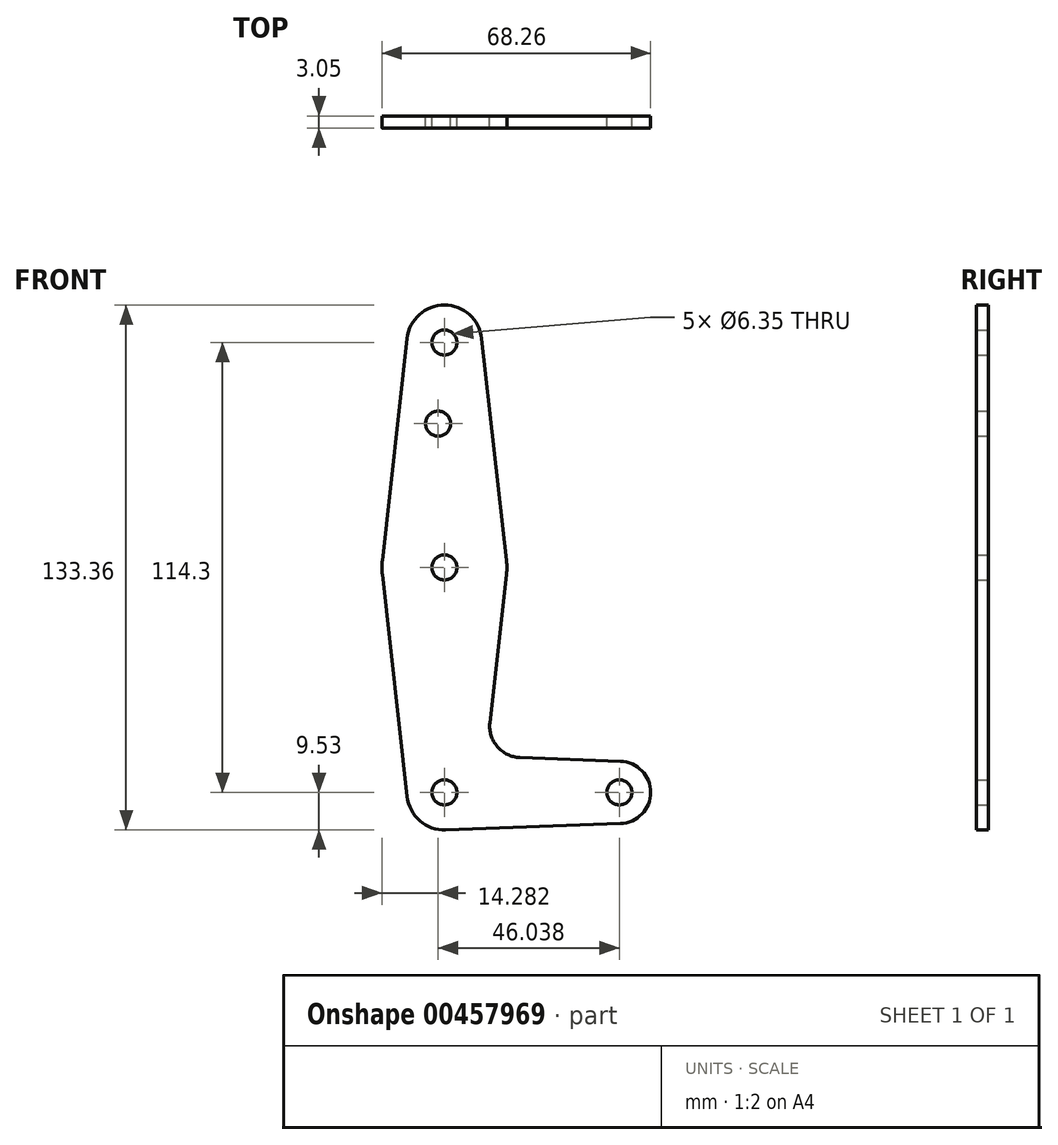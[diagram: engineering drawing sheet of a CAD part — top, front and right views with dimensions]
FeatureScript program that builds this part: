
annotation { "Feature Type Name" : "Feature", "Feature Type Description" : "" }
export const myFeature = defineFeature(function(context is Context, id is Id, definition is map)
    precondition{}
    {
        {
            var Q0;
            Q0=qCreatedBy(makeId("Front.planeOp"),FACE);
            var sketch = newSketch(context, id + "F0", { "sketchPlane" : qUnion([Q0])});
            skLineSegment(sketch, "E0", {"start": v(0, 0) * mm, "end": v(0, 114.3) * mm, "construction": true});
            skLineSegment(sketch, "E1", {"start": v(0, 0) * mm, "end": v(44.45, 0) * mm, "construction": true});
            skCircle(sketch, "E2", {"center": v(0, 114.3) * mm, "radius": 9.53 * mm});
            skCircle(sketch, "E3", {"center": v(44.45, 0) * mm, "radius": 7.94 * mm});
            skCircle(sketch, "E4", {"center": v(0, 0) * mm, "radius": 9.53 * mm});
            skCircle(sketch, "E5", {"center": v(0, 57.15) * mm, "radius": 15.88 * mm});
            skLineSegment(sketch, "E6", {"start": v(-9.47, 115.36) * mm, "end": v(-15.78, 58.91) * mm});
            skLineSegment(sketch, "E7", {"start": v(-15.78, 55.39) * mm, "end": v(-9.47, -1.06) * mm});
            skLineSegment(sketch, "E8", {"start": v(44.73, -7.93) * mm, "end": v(-3.54, -9.66) * mm});
            skLineSegment(sketch, "E9.MirrorCS", {"start": v(9.47, 115.36) * mm, "end": v(15.78, 58.91) * mm});
            skLineSegment(sketch, "E10.MirrorCS", {"start": v(15.78, 55.39) * mm, "end": v(11.56, 17.67) * mm});
            skLineSegment(sketch, "E11.MirrorCS", {"start": v(44.73, 7.93) * mm, "end": v(19.18, 8.85) * mm});
            skCircle(sketch, "E12", {"center": v(0, 114.3) * mm, "radius": 3.18 * mm});
            skCircle(sketch, "E13", {"center": v(-1.59, 93.68) * mm, "radius": 3.18 * mm});
            skCircle(sketch, "E14", {"center": v(0, 57.15) * mm, "radius": 3.18 * mm});
            skCircle(sketch, "E15", {"center": v(0, 0) * mm, "radius": 3.18 * mm});
            skCircle(sketch, "E16", {"center": v(44.45, 0) * mm, "radius": 3.18 * mm});
            skPoint(sketch, "E17.newPointA", {"position": v(9.47, -1.06) * mm});
            skPoint(sketch, "E17.newPointB", {"position": v(-3.54, 9.66) * mm});
            skArc(sketch, "E17.filletArc", {"start": v(11.56, 17.67) * mm, "mid": v(13.44, 11.6) * mm, "end": v(19.18, 8.85) * mm});
            skSolve(sketch);
        }
        {
            var Q0;
            Q0=makeQuery(id+"F0.imprint","IMPRINT",FACE,{"disambiguationData":[TD([[makeQuery(id+"F0.imprint","IMPRINT",EDGE,{"derivedFrom":sQuery(id+"F0.wireOp",EDGE,"E12")}),-1.0]])]});
            var Q1;
            {var subQ1=sQuery(id+"F0.wireOp",EDGE,"E6");Q1=makeQuery(id+"F0.imprint","IMPRINT",FACE,{"disambiguationData":[TD([[makeQuery(id+"F0.imprint","IMPRINT",EDGE,{"derivedFrom":subQ1}),1.0]])]});}
            var Q2;
            Q2=makeQuery(id+"F0.imprint","IMPRINT",FACE,{"disambiguationData":[TD([[makeQuery(id+"F0.imprint","IMPRINT",EDGE,{"derivedFrom":sQuery(id+"F0.wireOp",EDGE,"E14")}),-1.0]])]});
            var Q3;
            {var subQ0=sQuery(id+"F0.wireOp",EDGE,"E7");Q3=makeQuery(id+"F0.imprint","IMPRINT",FACE,{"disambiguationData":[TD([[makeQuery(id+"F0.imprint","IMPRINT",EDGE,{"derivedFrom":subQ0}),1.0]])]});}
            var Q4;
            Q4=makeQuery(id+"F0.imprint","IMPRINT",FACE,{"disambiguationData":[TD([[makeQuery(id+"F0.imprint","IMPRINT",EDGE,{"derivedFrom":sQuery(id+"F0.wireOp",EDGE,"E15")}),-1.0]])]});
            var Q5;
            Q5=makeQuery(id+"F0.imprint","IMPRINT",FACE,{"disambiguationData":[TD([[makeQuery(id+"F0.imprint","IMPRINT",EDGE,{"derivedFrom":sQuery(id+"F0.wireOp",EDGE,"E16")}),-1.0]])]});
            extrude(context, id + "F1", {"entities" : qUnion([Q0, Q1, Q2, Q3, Q4, Q5]), "depth" : 3.05 * mm});
        }
    });
